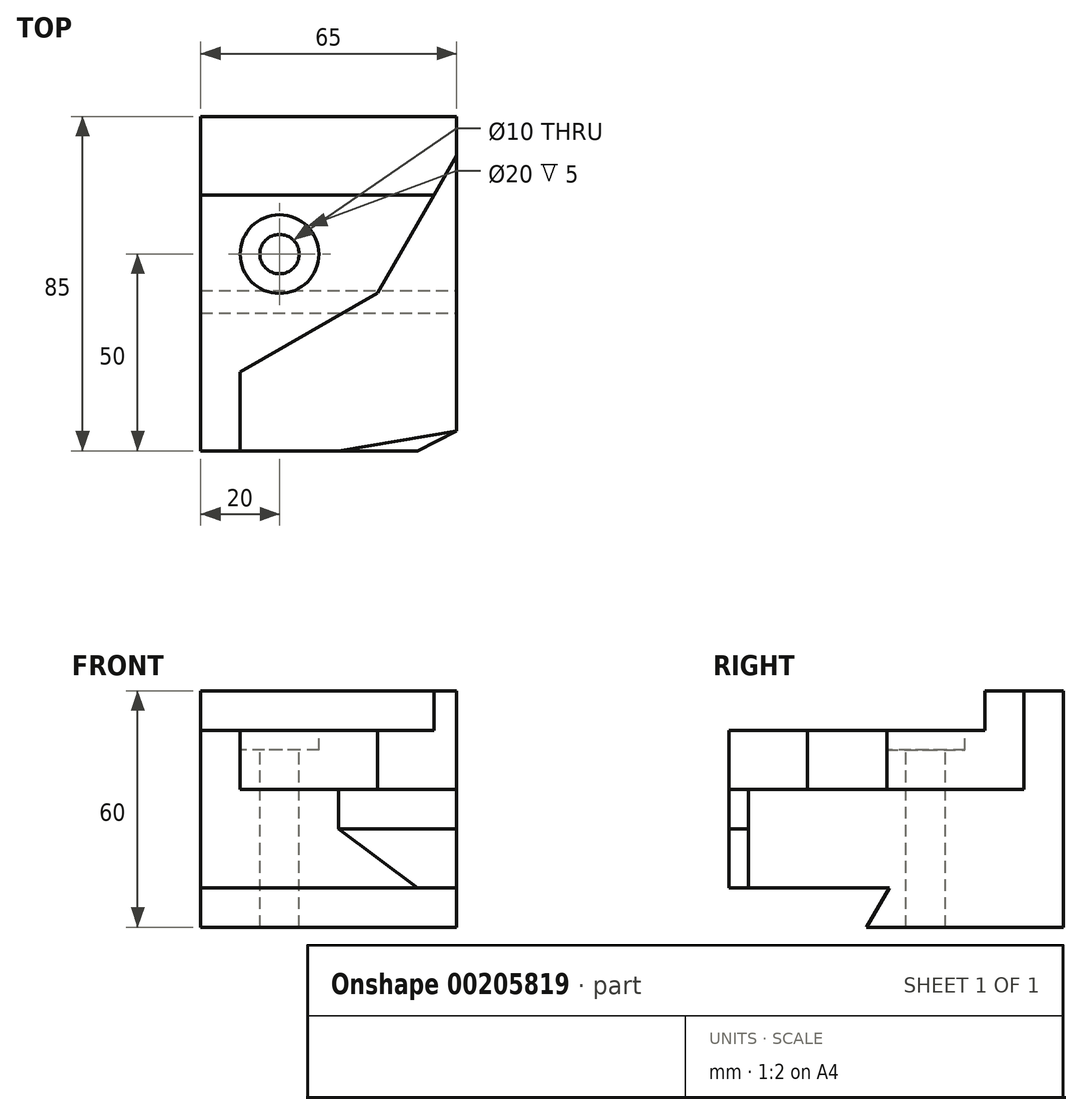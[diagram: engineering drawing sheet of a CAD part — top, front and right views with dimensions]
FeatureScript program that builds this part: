
annotation { "Feature Type Name" : "Feature", "Feature Type Description" : "" }
export const myFeature = defineFeature(function(context is Context, id is Id, definition is map)
    precondition{}
    {
        {
            var Q0;
            Q0=qCreatedBy(makeId("Top.planeOp"),FACE);
            var sketch = newSketch(context, id + "F0", { "sketchPlane" : qUnion([Q0])});
            skLineSegment(sketch, "E0.bottom", {"start": v(32.5, -42.5) * mm, "end": v(-32.5, -42.5) * mm});
            skLineSegment(sketch, "E0.top", {"start": v(32.5, 42.5) * mm, "end": v(-32.5, 42.5) * mm});
            skLineSegment(sketch, "E0.left", {"start": v(32.5, -42.5) * mm, "end": v(32.5, 42.5) * mm});
            skLineSegment(sketch, "E0.right", {"start": v(-32.5, -42.5) * mm, "end": v(-32.5, 42.5) * mm});
            skPoint(sketch, "E0.middle", {"position": v(0, 0) * mm});
            skSolve(sketch);
        }
        {
            var Q0;
            Q0=makeQuery(id+"F0.imprint","IMPRINT",FACE,{"disambiguationData":[TD([[makeQuery(id+"F0.imprint","IMPRINT",EDGE,{"derivedFrom":sQuery(id+"F0.wireOp",EDGE,"E0.bottom")}),-1.0]])]});
            extrude(context, id + "F1", {"entities" : qUnion([Q0]), "depth" : 25 * mm});
        }
        {
            var Q0;
            Q0=makeQuery(id+"F1.opExtrude","CAP_FACE",FACE,{"disambiguationData":[OSD([sQuery(id+"F0.wireOp",EDGE,"E0.bottom"),sQuery(id+"F0.wireOp",EDGE,"E0.top"),sQuery(id+"F0.wireOp",EDGE,"E0.left"),sQuery(id+"F0.wireOp",EDGE,"E0.right")])],"isStart":false});
            var sketch = newSketch(context, id + "F2", { "sketchPlane" : qUnion([Q0])});
            skLineSegment(sketch, "E1", {"start": v(-22.5, -42.5) * mm, "end": v(-22.5, -22.5) * mm});
            skLineSegment(sketch, "E2", {"start": v(-22.5, -22.5) * mm, "end": v(12.37, -2.37) * mm});
            skLineSegment(sketch, "E3", {"start": v(12.37, -2.37) * mm, "end": v(32.5, 32.5) * mm});
            skLineSegment(sketch, "E4", {"start": v(32.5, 32.5) * mm, "end": v(32.5, 42.5) * mm});
            skLineSegment(sketch, "E5", {"start": v(32.5, 42.5) * mm, "end": v(-32.5, 42.5) * mm});
            skLineSegment(sketch, "E6", {"start": v(-32.5, 42.5) * mm, "end": v(-32.5, -42.5) * mm});
            skLineSegment(sketch, "E7", {"start": v(-32.5, -42.5) * mm, "end": v(-22.5, -42.5) * mm});
            skSolve(sketch);
        }
        {
            var Q0;
            Q0 = qSketchRegion(id + "F2", true);
            extrude(context, id + "F3", {"entities" : qUnion([Q0]), "operationType" : NewBodyOperationType.ADD, "depth" : 15 * mm});
        }
        {
            var Q0;
            Q0=makeQuery(id+"F3.opExtrude","CAP_FACE",FACE,{"disambiguationData":[OSD([sQuery(id+"F2.wireOp",EDGE,"E1"),sQuery(id+"F2.wireOp",EDGE,"E2"),sQuery(id+"F2.wireOp",EDGE,"E3"),sQuery(id+"F2.wireOp",EDGE,"E4"),sQuery(id+"F2.wireOp",EDGE,"E5"),sQuery(id+"F2.wireOp",EDGE,"E6"),sQuery(id+"F2.wireOp",EDGE,"E7")])],"isStart":false});
            var sketch = newSketch(context, id + "F4", { "sketchPlane" : qUnion([Q0])});
            skLineSegment(sketch, "E8", {"start": v(-32.5, 22.5) * mm, "end": v(26.73, 22.5) * mm});
            skLineSegment(sketch, "E9", {"start": v(26.73, 22.5) * mm, "end": v(32.5, 32.5) * mm});
            skLineSegment(sketch, "E10", {"start": v(32.5, 32.5) * mm, "end": v(32.5, 42.5) * mm});
            skLineSegment(sketch, "E11", {"start": v(32.5, 42.5) * mm, "end": v(-32.5, 42.5) * mm});
            skLineSegment(sketch, "E12", {"start": v(-32.5, 42.5) * mm, "end": v(-32.5, 22.5) * mm});
            skSolve(sketch);
        }
        {
            var Q0;
            Q0 = qSketchRegion(id + "F4", true);
            extrude(context, id + "F5", {"entities" : qUnion([Q0]), "operationType" : NewBodyOperationType.ADD, "depth" : 10 * mm});
        }
        {
            var Q0;
            Q0=makeQuery(id+"F1.opExtrude","CAP_FACE",FACE,{"disambiguationData":[OSD([sQuery(id+"F0.wireOp",EDGE,"E0.bottom"),sQuery(id+"F0.wireOp",EDGE,"E0.top"),sQuery(id+"F0.wireOp",EDGE,"E0.left"),sQuery(id+"F0.wireOp",EDGE,"E0.right")])],"isStart":true});
            var sketch = newSketch(context, id + "F6", { "sketchPlane" : qUnion([Q0])});
            skLineSegment(sketch, "E13", {"start": v(22.5, 42.5) * mm, "end": v(32.5, 37.5) * mm});
            skLineSegment(sketch, "E14", {"start": v(32.5, 37.5) * mm, "end": v(32.5, 42.5) * mm});
            skLineSegment(sketch, "E15", {"start": v(32.5, 42.5) * mm, "end": v(22.5, 42.5) * mm});
            skSolve(sketch);
        }
        {
            var Q0;
            Q0=makeQuery(id+"F3.boolean.opBoolean","MERGE",FACE,{"derivedFrom":[makeQuery(id+"F1.opExtrude","SWEPT_FACE",FACE,{"disambiguationData":[OSD([sQuery(id+"F0.wireOp",EDGE,"E0.bottom")])]}),makeQuery(id+"F3.opExtrude","SWEPT_FACE",FACE,{"disambiguationData":[OSD([sQuery(id+"F2.wireOp",EDGE,"E7")])]})]});
            var sketch = newSketch(context, id + "F7", { "sketchPlane" : qUnion([Q0])});
            skLineSegment(sketch, "E16", {"start": v(2.5, 25) * mm, "end": v(2.5, 15) * mm});
            skSolve(sketch);
        }
        {
            var Q0;
            Q0=makeQuery(id+"F1.opExtrude","CAP_FACE",FACE,{"disambiguationData":[OSD([sQuery(id+"F0.wireOp",EDGE,"E0.bottom"),sQuery(id+"F0.wireOp",EDGE,"E0.top"),sQuery(id+"F0.wireOp",EDGE,"E0.left"),sQuery(id+"F0.wireOp",EDGE,"E0.right")])],"isStart":false});
            var sketch = newSketch(context, id + "F8", { "sketchPlane" : qUnion([Q0])});
            skPoint(sketch, "E17.0", {"position": v(2.5, -42.5) * mm});
            skLineSegment(sketch, "E18", {"start": v(2.5, -42.5) * mm, "end": v(32.5, -37.5) * mm});
            skLineSegment(sketch, "E19", {"start": v(2.5, -42.5) * mm, "end": v(32.5, -42.5) * mm});
            skLineSegment(sketch, "E20", {"start": v(32.5, -42.5) * mm, "end": v(32.5, -37.5) * mm});
            skSolve(sketch);
        }
        {
            var Q0;
            Q0=makeQuery(id+"F8.imprint","IMPRINT",FACE,{"disambiguationData":[TD([[makeQuery(id+"F8.imprint","IMPRINT",EDGE,{"derivedFrom":sQuery(id+"F8.wireOp",EDGE,"E18")}),-1.0]])]});
            extrude(context, id + "F9", {"entities" : qUnion([Q0]), "operationType" : NewBodyOperationType.REMOVE, "oppositeDirection" : true, "depth" : 10 * mm});
        }
        {
            var Q1;
            Q1=makeQuery(id+"F9.boolean.opBoolean","COPY",FACE,{"derivedFrom":makeQuery(id+"F9.opExtrude","CAP_FACE",FACE,{"disambiguationData":[OSD([sQuery(id+"F8.wireOp",EDGE,"E18"),sQuery(id+"F8.wireOp",EDGE,"E19"),sQuery(id+"F8.wireOp",EDGE,"E20")])],"isStart":false})});
            var Q2;
            Q2=makeQuery(id+"F6.imprint","IMPRINT",FACE,{"disambiguationData":[TD([[makeQuery(id+"F6.imprint","IMPRINT",EDGE,{"derivedFrom":sQuery(id+"F6.wireOp",EDGE,"E13")}),1.0]])]});
            loft(context, id + "F10", {"operationType" : NewBodyOperationType.REMOVE, "sheetProfilesArray" : [{ "sheetProfileEntities" : qUnion([Q1]) }, { "sheetProfileEntities" : qUnion([Q2]) }]});
        }
        {
            var Q0;
            Q0=makeQuery(id+"F5.boolean.opBoolean","MERGE",FACE,{"derivedFrom":[makeQuery(id+"F3.boolean.opBoolean","MERGE",FACE,{"derivedFrom":[makeQuery(id+"F1.opExtrude","SWEPT_FACE",FACE,{"disambiguationData":[OSD([sQuery(id+"F0.wireOp",EDGE,"E0.left")])]}),makeQuery(id+"F3.opExtrude","SWEPT_FACE",FACE,{"disambiguationData":[OSD([sQuery(id+"F2.wireOp",EDGE,"E4")])]})]}),makeQuery(id+"F5.opExtrude","SWEPT_FACE",FACE,{"disambiguationData":[OSD([sQuery(id+"F4.wireOp",EDGE,"E10")])]})]});
            var sketch = newSketch(context, id + "F11", { "sketchPlane" : qUnion([Q0])});
            skLineSegment(sketch, "E21", {"start": v(42.5, 0) * mm, "end": v(42.5, -10) * mm});
            skLineSegment(sketch, "E22", {"start": v(42.5, -10) * mm, "end": v(-7.5, -10) * mm});
            skLineSegment(sketch, "E23", {"start": v(-7.5, -10) * mm, "end": v(-1.73, 0) * mm});
            skLineSegment(sketch, "E24", {"start": v(-1.73, 0) * mm, "end": v(42.5, 0) * mm});
            skSolve(sketch);
        }
        {
            var Q0;
            Q0=makeQuery(id+"F11.imprint","IMPRINT",FACE,{"disambiguationData":[TD([[makeQuery(id+"F11.imprint","IMPRINT",EDGE,{"derivedFrom":sQuery(id+"F11.wireOp",EDGE,"E21")}),-1.0]])]});
            var Q1;
            Q1=makeQuery(id+"F5.boolean.opBoolean","MERGE",FACE,{"derivedFrom":[makeQuery(id+"F3.boolean.opBoolean","MERGE",FACE,{"derivedFrom":[makeQuery(id+"F1.opExtrude","SWEPT_FACE",FACE,{"disambiguationData":[OSD([sQuery(id+"F0.wireOp",EDGE,"E0.right")])]}),makeQuery(id+"F3.opExtrude","SWEPT_FACE",FACE,{"disambiguationData":[OSD([sQuery(id+"F2.wireOp",EDGE,"E6")])]})]}),makeQuery(id+"F5.opExtrude","SWEPT_FACE",FACE,{"disambiguationData":[OSD([sQuery(id+"F4.wireOp",EDGE,"E12")])]})]});
            extrude(context, id + "F12", {"entities" : qUnion([Q0]), "operationType" : NewBodyOperationType.ADD, "endBound" : BoundingType.UP_TO_SURFACE, "oppositeDirection" : true, "endBoundEntityFace" : qUnion([Q1]), "depth" : 25 * mm});
        }
        {
            var Q0;
            Q0=makeQuery(id+"F3.opExtrude","CAP_FACE",FACE,{"disambiguationData":[OSD([sQuery(id+"F2.wireOp",EDGE,"E1"),sQuery(id+"F2.wireOp",EDGE,"E2"),sQuery(id+"F2.wireOp",EDGE,"E3"),sQuery(id+"F2.wireOp",EDGE,"E4"),sQuery(id+"F2.wireOp",EDGE,"E5"),sQuery(id+"F2.wireOp",EDGE,"E6"),sQuery(id+"F2.wireOp",EDGE,"E7")])],"isStart":false});
            var sketch = newSketch(context, id + "F13", { "sketchPlane" : qUnion([Q0])});
            skPoint(sketch, "E25", {"position": v(-12.5, 7.5) * mm});
            skSolve(sketch);
        }
        {
            var Q0;
            Q0=sQuery(id+"F13.wireOp",VERTEX,"E25");
            var Q1;
            Q1=makeQuery(id+"F1.opExtrude","SWEPT_BODY",BODY,{"disambiguationData":[OSD([sQuery(id+"F0.wireOp",EDGE,"E0.bottom"),sQuery(id+"F0.wireOp",EDGE,"E0.top"),sQuery(id+"F0.wireOp",EDGE,"E0.left"),sQuery(id+"F0.wireOp",EDGE,"E0.right")])]});
            hole(context, id + "F14", {"style" : HoleStyle.C_BORE, "endStyle" : HoleEndStyle.THROUGH, "holeDiameter" : 10 * mm, "cBoreDiameter" : 20 * mm, "cBoreDepth" : 5 * mm, "isTappedThrough" : true, "tappedDepth" : 12 * mm, "tapClearance" : 3, "locations" : qUnion([Q0]), "scope" : qUnion([Q1])});
        }
    });
